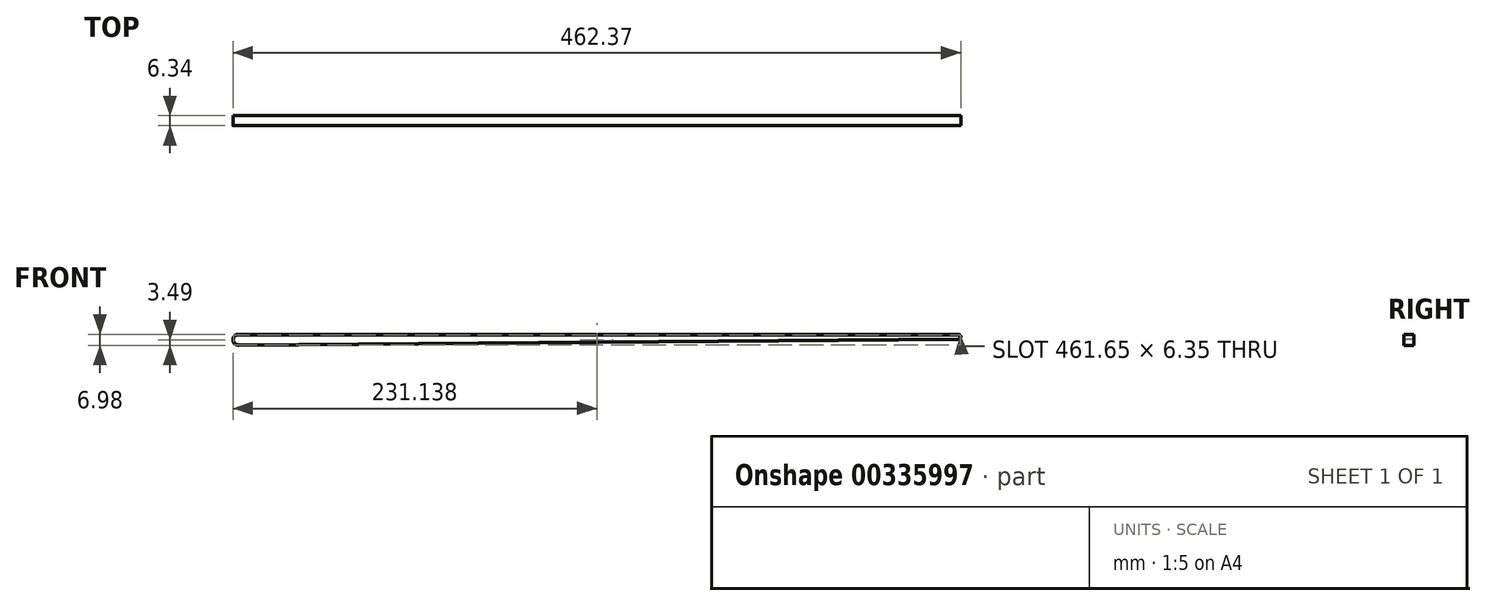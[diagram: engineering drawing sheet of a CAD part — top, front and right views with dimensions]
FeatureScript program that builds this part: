
annotation { "Feature Type Name" : "Feature", "Feature Type Description" : "" }
export const myFeature = defineFeature(function(context is Context, id is Id, definition is map)
    precondition{}
    {
        {
            var Q0;
            Q0=qCreatedBy(makeId("Front.planeOp"),FACE);
            var sketch = newSketch(context, id + "F0", { "sketchPlane" : qUnion([Q0])});
            skArc(sketch, "E0", {"start": v(0, 3.5) * mm, "mid": v(-3.5, -0.03) * mm, "end": v(0.06, -3.5) * mm});
            skArc(sketch, "E1", {"start": v(0, 3.18) * mm, "mid": v(-3.17, -0.01) * mm, "end": v(0.03, -3.17) * mm});
            skArc(sketch, "E2", {"start": v(457.2, 0.55) * mm, "mid": v(458.47, 1.82) * mm, "end": v(457.2, 3.09) * mm});
            skArc(sketch, "E3", {"start": v(457.21, 0.14) * mm, "mid": v(458.88, 1.82) * mm, "end": v(457.2, 3.5) * mm});
            skLineSegment(sketch, "E4", {"start": v(457.2, 3.5) * mm, "end": v(0, 3.5) * mm});
            skLineSegment(sketch, "E5", {"start": v(457.2, 3.09) * mm, "end": v(0, 3.18) * mm});
            skLineSegment(sketch, "E6", {"start": v(457.2, 0.55) * mm, "end": v(0, -3.18) * mm});
            skLineSegment(sketch, "E7", {"start": v(0, -3.5) * mm, "end": v(457.21, 0.14) * mm});
            skSolve(sketch);
        }
        {
            var Q0;
            {var subQ8=sQuery(id+"F0.wireOp",EDGE,"E2");Q0=makeQuery(id+"F0.imprint","IMPRINT",FACE,{"disambiguationData":[TD([[makeQuery(id+"F0.imprint","IMPRINT",EDGE,{"derivedFrom":subQ8}),-1.0]])]});}
            extrude(context, id + "F1", {"entities" : qUnion([Q0]), "endBound" : BoundingType.SYMMETRIC, "depth" : 6.35 * mm});
        }
    });
